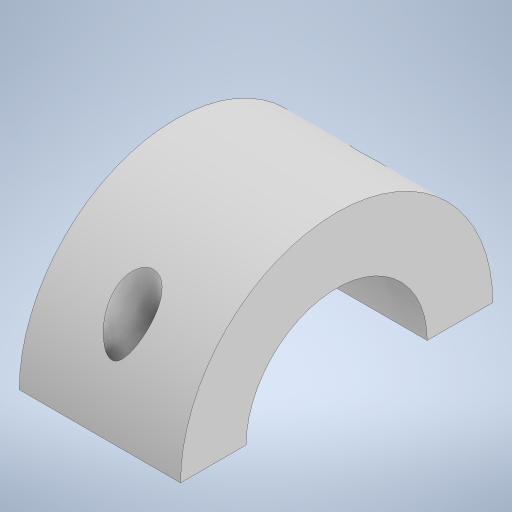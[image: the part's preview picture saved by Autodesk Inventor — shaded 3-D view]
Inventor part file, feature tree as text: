
AUTODESK INVENTOR PART (.ipt)
format: ipt  version: 2023 (Build 270158000, 158)  size: 235,520 bytes
history: native  units: mm
features: extrude x2, sketch x2, projected_geometry x2, plane x1
ambient origin geometry x8: Origin, YZ Plane, XZ Plane, XY Plane, X Axis, Y Axis, Z Axis, Center Point
bodies: Solid1 (feature_tree)
feature tree (7):
  extrude  "Extrusion1"  Depth=30.0mm
  plane  "Work Plane1"
  extrude  "Extrusion2"  Depth=6.3mm
  sketch  "Sketch1"  dims[d0=17.4mm d1=30.0mm]
  sketch  "Sketch2"  dims[d2=6.3mm d3=6.3mm d4=15.5mm d5=0.0mm d6=4.0mm d7=4.0mm d8=0.0mm d9=0.0mm]
  projected_geometry  "Projected Loop1"
  projected_geometry  "Projected Loop2"
